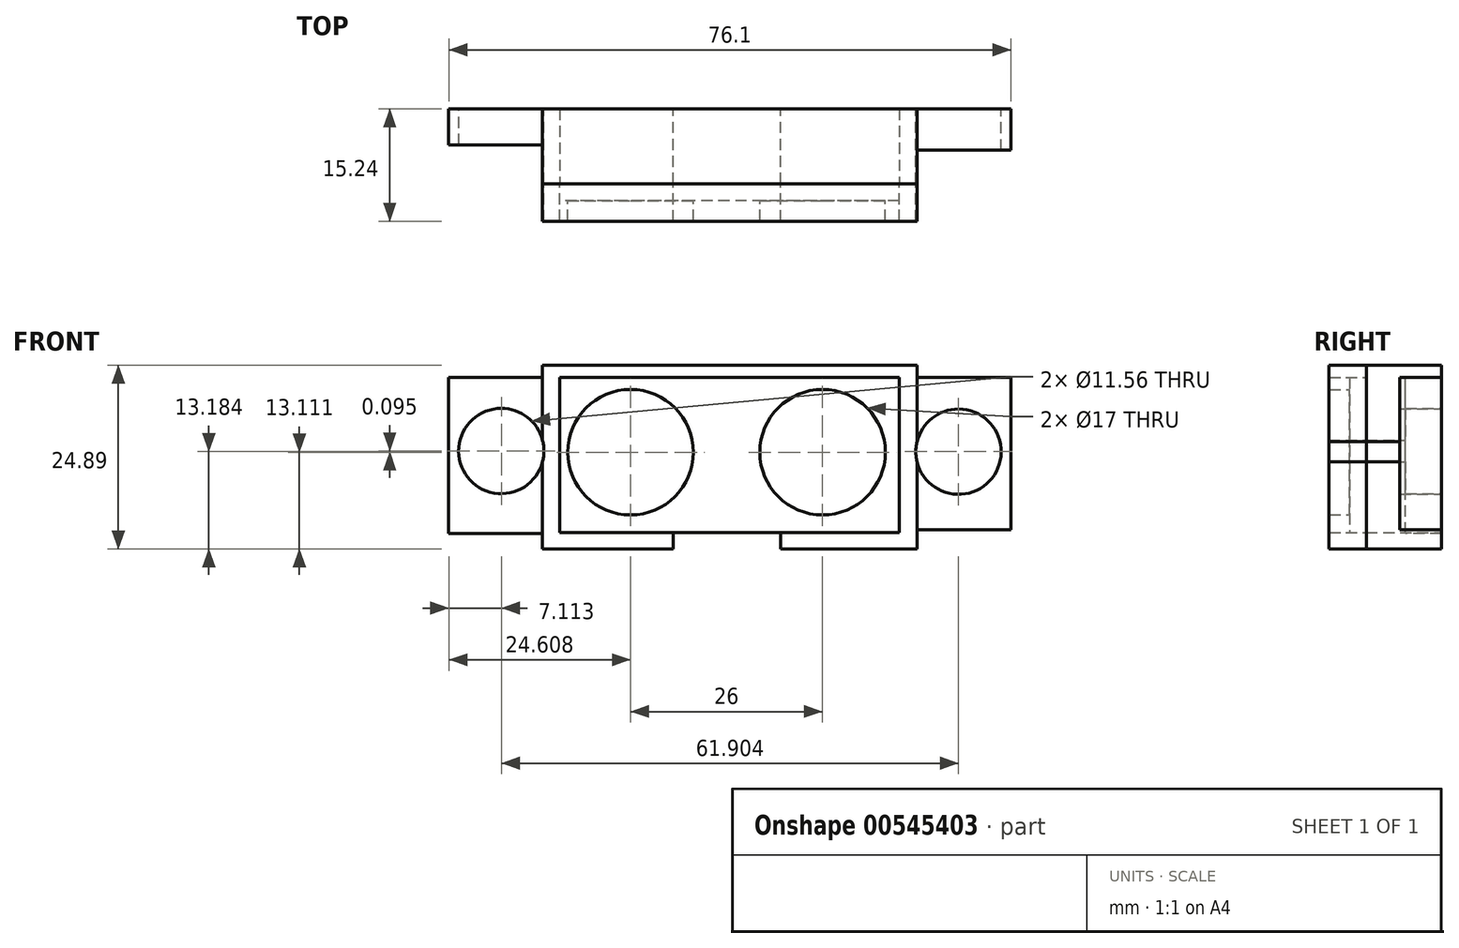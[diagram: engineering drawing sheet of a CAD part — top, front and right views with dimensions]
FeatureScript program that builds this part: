
annotation { "Feature Type Name" : "Feature", "Feature Type Description" : "" }
export const myFeature = defineFeature(function(context is Context, id is Id, definition is map)
    precondition{}
    {
        {
            var Q0;
            Q0=qCreatedBy(makeId("Front.planeOp"),FACE);
            var sketch = newSketch(context, id + "F0", { "sketchPlane" : qUnion([Q0])});
            skLineSegment(sketch, "E0", {"start": v(0, 0) * mm, "end": v(0, -21) * mm});
            skLineSegment(sketch, "E1.bottom", {"start": v(0, 0) * mm, "end": v(-46, 0) * mm});
            skLineSegment(sketch, "E1.top", {"start": v(0, -21) * mm, "end": v(-46, -21) * mm});
            skLineSegment(sketch, "E1.right", {"start": v(-46, 0) * mm, "end": v(-46, -21) * mm});
            skCircle(sketch, "E2", {"center": v(-36.4, -10.12) * mm, "radius": 8.5 * mm});
            skCircle(sketch, "E3", {"center": v(-10.4, -10.12) * mm, "radius": 8.5 * mm});
            skSolve(sketch);
        }
        {
            var Q0;
            Q0=makeQuery(id+"F0.imprint","IMPRINT",FACE,{"disambiguationData":[TD([[makeQuery(id+"F0.imprint","IMPRINT",EDGE,{"derivedFrom":sQuery(id+"F0.wireOp",EDGE,"E1.bottom")}),1.0]])]});
            extrude(context, id + "F1", {"entities" : qUnion([Q0]), "flatOperationType" : FlatOperationType.REMOVE, "depth" : 5 * mm, "offsetDistance" : 25.4 * mm, "domain" : OperationDomain.MODEL});
        }
        {
            var Q0;
            Q0=makeQuery(id+"F1.opExtrude","CAP_FACE",FACE,{"disambiguationData":[OSD([sQuery(id+"F0.wireOp",EDGE,"E1.bottom"),sQuery(id+"F0.wireOp",EDGE,"E1.top"),sQuery(id+"F0.wireOp",EDGE,"E0"),sQuery(id+"F0.wireOp",EDGE,"E1.right"),sQuery(id+"F0.wireOp",EDGE,"E2"),sQuery(id+"F0.wireOp",EDGE,"E3")])],"isStart":true});
            var sketch = newSketch(context, id + "F2", { "sketchPlane" : qUnion([Q0])});
            skLineSegment(sketch, "E4.bottom", {"start": v(0, 0) * mm, "end": v(46, 0) * mm});
            skLineSegment(sketch, "E4.top", {"start": v(0, -21) * mm, "end": v(46, -21) * mm});
            skLineSegment(sketch, "E4.left", {"start": v(0, 0) * mm, "end": v(0, -21) * mm});
            skLineSegment(sketch, "E4.right", {"start": v(46, 0) * mm, "end": v(46, -21) * mm});
            skLineSegment(sketch, "E5.bottom", {"start": v(-2.4, 1.66) * mm, "end": v(48.3, 1.66) * mm});
            skLineSegment(sketch, "E5.top", {"start": v(-2.4, -23.23) * mm, "end": v(48.3, -23.23) * mm});
            skLineSegment(sketch, "E5.left", {"start": v(-2.4, 1.66) * mm, "end": v(-2.4, -23.23) * mm});
            skLineSegment(sketch, "E5.right", {"start": v(48.3, 1.66) * mm, "end": v(48.3, -23.23) * mm});
            skSolve(sketch);
        }
        {
            var Q0;
            Q0 = qSketchRegion(id + "F2", true);
            extrude(context, id + "F3", {"entities" : qUnion([Q0]), "flatOperationType" : FlatOperationType.REMOVE, "depth" : 25.4 * mm, "offsetDistance" : 25.4 * mm, "domain" : OperationDomain.MODEL});
        }
        {
            var Q0;
            Q0=makeQuery(id+"F3.opExtrude","SWEPT_FACE",FACE,{"disambiguationData":[OSD([sQuery(id+"F2.wireOp",EDGE,"E4.top")])]});
            var sketch = newSketch(context, id + "F4", { "sketchPlane" : qUnion([Q0])});
            skLineSegment(sketch, "E6.bottom", {"start": v(-16.08, 0) * mm, "end": v(-30.6, 0) * mm});
            skLineSegment(sketch, "E6.top", {"start": v(-16.08, 25.4) * mm, "end": v(-30.6, 25.4) * mm});
            skLineSegment(sketch, "E6.left", {"start": v(-16.08, 0) * mm, "end": v(-16.08, 25.4) * mm});
            skLineSegment(sketch, "E6.right", {"start": v(-30.6, 0) * mm, "end": v(-30.6, 25.4) * mm});
            skSolve(sketch);
        }
        {
            var Q0;
            Q0 = qSketchRegion(id + "F4", true);
            extrude(context, id + "F5", {"entities" : qUnion([Q0]), "operationType" : NewBodyOperationType.REMOVE, "flatOperationType" : FlatOperationType.REMOVE, "oppositeDirection" : true, "depth" : 14.73 * mm, "offsetDistance" : 25.4 * mm, "domain" : OperationDomain.MODEL});
        }
        {
            var Q0;
            Q0=makeQuery(id+"F3.opExtrude","CAP_FACE",FACE,{"disambiguationData":[OSD([sQuery(id+"F2.wireOp",EDGE,"E4.bottom"),sQuery(id+"F2.wireOp",EDGE,"E4.top"),sQuery(id+"F2.wireOp",EDGE,"E4.left"),sQuery(id+"F2.wireOp",EDGE,"E4.right"),sQuery(id+"F2.wireOp",EDGE,"E5.bottom"),sQuery(id+"F2.wireOp",EDGE,"E5.top"),sQuery(id+"F2.wireOp",EDGE,"E5.left"),sQuery(id+"F2.wireOp",EDGE,"E5.right")])],"isStart":false});
            var sketch = newSketch(context, id + "F6", { "sketchPlane" : qUnion([Q0])});
            skLineSegment(sketch, "E7.bottom", {"start": v(-2.4, 1.66) * mm, "end": v(48.3, 1.66) * mm});
            skLineSegment(sketch, "E7.top", {"start": v(-2.4, -23.23) * mm, "end": v(48.3, -23.23) * mm});
            skLineSegment(sketch, "E7.left", {"start": v(-2.4, 1.66) * mm, "end": v(-2.4, -23.23) * mm});
            skLineSegment(sketch, "E7.right", {"start": v(48.3, 1.66) * mm, "end": v(48.3, -23.23) * mm});
            skSolve(sketch);
        }
        {
            var Q0;
            Q0 = qSketchRegion(id + "F6", true);
            extrude(context, id + "F7", {"entities" : qUnion([Q0]), "operationType" : NewBodyOperationType.REMOVE, "flatOperationType" : FlatOperationType.REMOVE, "oppositeDirection" : true, "depth" : 10.16 * mm, "offsetDistance" : 25.4 * mm, "domain" : OperationDomain.MODEL});
        }
        {
            var Q0;
            Q0=makeQuery(id+"F3.opExtrude","CAP_FACE",FACE,{"disambiguationData":[OSD([sQuery(id+"F2.wireOp",EDGE,"E4.bottom"),sQuery(id+"F2.wireOp",EDGE,"E4.top"),sQuery(id+"F2.wireOp",EDGE,"E4.left"),sQuery(id+"F2.wireOp",EDGE,"E4.right"),sQuery(id+"F2.wireOp",EDGE,"E5.bottom"),sQuery(id+"F2.wireOp",EDGE,"E5.top"),sQuery(id+"F2.wireOp",EDGE,"E5.left"),sQuery(id+"F2.wireOp",EDGE,"E5.right")])],"isStart":true});
            var sketch = newSketch(context, id + "F8", { "sketchPlane" : qUnion([Q0])});
            skLineSegment(sketch, "E8", {"start": v(-48.3, -23.23) * mm, "end": v(2.4, -23.23) * mm});
            skLineSegment(sketch, "E9", {"start": v(2.4, -23.23) * mm, "end": v(2.4, 1.66) * mm});
            skLineSegment(sketch, "E10", {"start": v(2.4, 1.66) * mm, "end": v(-48.3, 1.66) * mm});
            skLineSegment(sketch, "E11", {"start": v(-48.3, 1.66) * mm, "end": v(-48.3, -23.23) * mm});
            skLineSegment(sketch, "E12", {"start": v(-46, -21) * mm, "end": v(-46, 0) * mm});
            skLineSegment(sketch, "E13", {"start": v(-46, 0) * mm, "end": v(0, 0) * mm});
            skLineSegment(sketch, "E14", {"start": v(0, 0) * mm, "end": v(0, -21) * mm});
            skLineSegment(sketch, "E15", {"start": v(0, -21) * mm, "end": v(-46, -21) * mm});
            skSolve(sketch);
        }
        {
            var Q0;
            {var subQ1=sQuery(id+"F4.wireOp",EDGE,"E6.bottom");var subQ2=sQuery(id+"F2.wireOp",EDGE,"E4.top");var subQ3=makeQuery(id+"F5.boolean.opBoolean","COPY",EDGE,{"derivedFrom":makeQuery(id+"F5.opExtrude","SWEPT_EDGE",EDGE,{"disambiguationData":[OSD([subQ2,subQ1,sQuery(id+"F4.wireOp",EDGE,"E6.left")])]})});Q0=makeQuery(id+"F8.imprint","IMPRINT",FACE,{"disambiguationData":[TD([[makeQuery(id+"F8.imprint","IMPRINT",EDGE,{"derivedFrom":subQ3}),1.0]])]});}
            var Q1;
            {var subQ8=sQuery(id+"F8.wireOp",EDGE,"E9");Q1=makeQuery(id+"F8.imprint","IMPRINT",FACE,{"disambiguationData":[TD([[makeQuery(id+"F8.imprint","IMPRINT",EDGE,{"derivedFrom":subQ8}),-1.0]])]});}
            extrude(context, id + "F9", {"entities" : qUnion([Q0, Q1]), "depth" : 5.08 * mm, "offsetDistance" : 25.4 * mm});
        }
        {
            var Q0;
            Q0=makeQuery(id+"F7.boolean.opBoolean","COPY",FACE,{"derivedFrom":makeQuery(id+"F7.opExtrude","CAP_FACE",FACE,{"disambiguationData":[OSD([sQuery(id+"F6.wireOp",EDGE,"E7.bottom"),sQuery(id+"F6.wireOp",EDGE,"E7.top"),sQuery(id+"F6.wireOp",EDGE,"E7.left"),sQuery(id+"F6.wireOp",EDGE,"E7.right")])],"isStart":false})});
            extrude(context, id + "F10", {"entities" : qUnion([Q0]), "operationType" : NewBodyOperationType.REMOVE, "oppositeDirection" : true, "depth" : 7.87 * mm, "offsetDistance" : 25.4 * mm});
        }
        {
            var Q0;
            Q0=makeQuery(id+"F1.opExtrude","CAP_FACE",FACE,{"disambiguationData":[OSD([sQuery(id+"F0.wireOp",EDGE,"E1.bottom"),sQuery(id+"F0.wireOp",EDGE,"E1.top"),sQuery(id+"F0.wireOp",EDGE,"E0"),sQuery(id+"F0.wireOp",EDGE,"E1.right"),sQuery(id+"F0.wireOp",EDGE,"E2"),sQuery(id+"F0.wireOp",EDGE,"E3")])],"isStart":true});
            extrude(context, id + "F11", {"entities" : qUnion([Q0]), "operationType" : NewBodyOperationType.REMOVE, "oppositeDirection" : true, "depth" : 2.3 * mm, "offsetDistance" : 25.4 * mm});
        }
        {
            var Q0;
            Q0=makeQuery(id+"F3.opExtrude","SWEPT_FACE",FACE,{"disambiguationData":[OSD([sQuery(id+"F2.wireOp",EDGE,"E5.right")])]});
            var sketch = newSketch(context, id + "F12", { "sketchPlane" : qUnion([Q0])});
            skLineSegment(sketch, "E16.bottom", {"start": v(-7.37, -21.13) * mm, "end": v(-5.29, -21.13) * mm});
            skLineSegment(sketch, "E16.top", {"start": v(-7.37, 0) * mm, "end": v(-5.29, 0) * mm});
            skLineSegment(sketch, "E16.left", {"start": v(-7.37, -21.13) * mm, "end": v(-7.37, 0) * mm});
            skLineSegment(sketch, "E16.right", {"start": v(-5.29, -21.13) * mm, "end": v(-5.29, 0) * mm});
            skSolve(sketch);
        }
        {
            var Q0;
            Q0=makeQuery(id+"F3.opExtrude","SWEPT_FACE",FACE,{"disambiguationData":[OSD([sQuery(id+"F2.wireOp",EDGE,"E5.left")])]});
            var sketch = newSketch(context, id + "F13", { "sketchPlane" : qUnion([Q0])});
            skLineSegment(sketch, "E17.bottom", {"start": v(7.37, 0) * mm, "end": v(4.56, 0) * mm});
            skLineSegment(sketch, "E17.top", {"start": v(7.37, -20.64) * mm, "end": v(4.56, -20.64) * mm});
            skLineSegment(sketch, "E17.left", {"start": v(7.37, 0) * mm, "end": v(7.37, -20.64) * mm});
            skLineSegment(sketch, "E17.right", {"start": v(4.56, 0) * mm, "end": v(4.56, -20.64) * mm});
            skSolve(sketch);
        }
        {
            var Q0;
            Q0=makeQuery(id+"F12.imprint","IMPRINT",FACE,{"disambiguationData":[TD([[makeQuery(id+"F12.imprint","IMPRINT",EDGE,{"derivedFrom":sQuery(id+"F12.wireOp",EDGE,"E16.bottom")}),1.0]])]});
            extrude(context, id + "F14", {"entities" : qUnion([Q0]), "operationType" : NewBodyOperationType.ADD, "depth" : 12.7 * mm, "offsetDistance" : 25.4 * mm});
        }
        {
            var Q0;
            Q0=makeQuery(id+"F13.imprint","IMPRINT",FACE,{"disambiguationData":[TD([[makeQuery(id+"F13.imprint","IMPRINT",EDGE,{"derivedFrom":sQuery(id+"F13.wireOp",EDGE,"E17.bottom")}),1.0]])]});
            extrude(context, id + "F15", {"entities" : qUnion([Q0]), "operationType" : NewBodyOperationType.ADD, "depth" : 12.7 * mm, "offsetDistance" : 25.4 * mm});
        }
        {
            var Q0;
            Q0=makeQuery(id+"F15.boolean.opBoolean","MERGE",FACE,{"derivedFrom":[makeQuery(id+"F14.boolean.opBoolean","MERGE",FACE,{"derivedFrom":[makeQuery(id+"F10.boolean.opBoolean","COPY",FACE,{"derivedFrom":makeQuery(id+"F10.opExtrude","CAP_FACE",FACE,{"disambiguationData":[OSD([sQuery(id+"F6.wireOp",EDGE,"E7.bottom"),sQuery(id+"F6.wireOp",EDGE,"E7.top"),sQuery(id+"F6.wireOp",EDGE,"E7.left"),sQuery(id+"F6.wireOp",EDGE,"E7.right")])],"isStart":false})}),makeQuery(id+"F14.opExtrude","SWEPT_FACE",FACE,{"disambiguationData":[OSD([sQuery(id+"F12.wireOp",EDGE,"E16.left")])]})]}),makeQuery(id+"F15.opExtrude","SWEPT_FACE",FACE,{"disambiguationData":[OSD([sQuery(id+"F13.wireOp",EDGE,"E17.left")])]})]});
            extrude(context, id + "F16", {"entities" : qUnion([Q0]), "operationType" : NewBodyOperationType.ADD, "depth" : 2.8 * mm, "offsetDistance" : 25.4 * mm});
        }
        {
            var Q0;
            Q0=makeQuery(id+"F16.opExtrude","CAP_FACE",FACE,{"disambiguationData":[OSD([sQuery(id+"F6.wireOp",EDGE,"E7.bottom"),sQuery(id+"F6.wireOp",EDGE,"E7.top"),sQuery(id+"F6.wireOp",EDGE,"E7.left"),sQuery(id+"F6.wireOp",EDGE,"E7.right"),sQuery(id+"F12.wireOp",EDGE,"E16.left"),sQuery(id+"F13.wireOp",EDGE,"E17.left")])],"isStart":false});
            var sketch = newSketch(context, id + "F17", { "sketchPlane" : qUnion([Q0])});
            skCircle(sketch, "E18", {"center": v(53.89, -9.95) * mm, "radius": 5.79 * mm});
            skCircle(sketch, "E19", {"center": v(53.89, -9.95) * mm, "radius": 5.78 * mm});
            skCircle(sketch, "E20", {"center": v(-8.02, -10.05) * mm, "radius": 5.78 * mm});
            skSolve(sketch);
        }
        {
            var Q0;
            Q0=makeQuery(id+"F17.imprint","IMPRINT",FACE,{"disambiguationData":[TD([[makeQuery(id+"F17.imprint","IMPRINT",EDGE,{"derivedFrom":sQuery(id+"F17.wireOp",EDGE,"E20")}),1.0]])]});
            var Q1;
            Q1=makeQuery(id+"F17.imprint","IMPRINT",FACE,{"disambiguationData":[TD([[makeQuery(id+"F17.imprint","IMPRINT",EDGE,{"derivedFrom":sQuery(id+"F17.wireOp",EDGE,"E19")}),1.0]])]});
            extrude(context, id + "F18", {"entities" : qUnion([Q0, Q1]), "operationType" : NewBodyOperationType.REMOVE, "oppositeDirection" : true, "depth" : 25.4 * mm, "offsetDistance" : 25.4 * mm});
        }
    });
